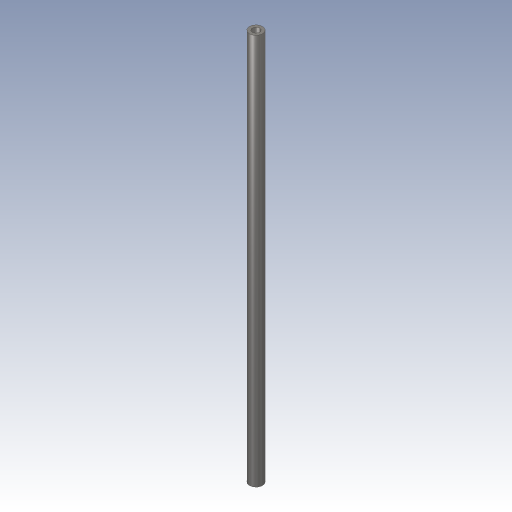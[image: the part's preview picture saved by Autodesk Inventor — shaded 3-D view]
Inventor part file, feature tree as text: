
AUTODESK INVENTOR PART (.ipt)
format: ipt  version: 2023.3 (Build 273359000, 359)  size: 132,608 bytes
history: native  units: in
note: dims shown in document units (in); Inventor stores cm internally (conversion verified against a paired STEP export)
features: extrude x1, sketch x1
ambient origin geometry x8: Origin, YZ Plane, XZ Plane, XY Plane, X Axis, Y Axis, Z Axis, Center Point
bodies: Body1 (feature_tree)
feature tree (2):
  extrude  "Extrusion4"  Depth=0.8268in
  sketch  "Skizze6"  dims[d30=0.0276in d31=0.0157in d32=0.8268in d33=0.0in d34=0.0197in d35=0.0344in d36=0.0197in d37=0.0344in]
